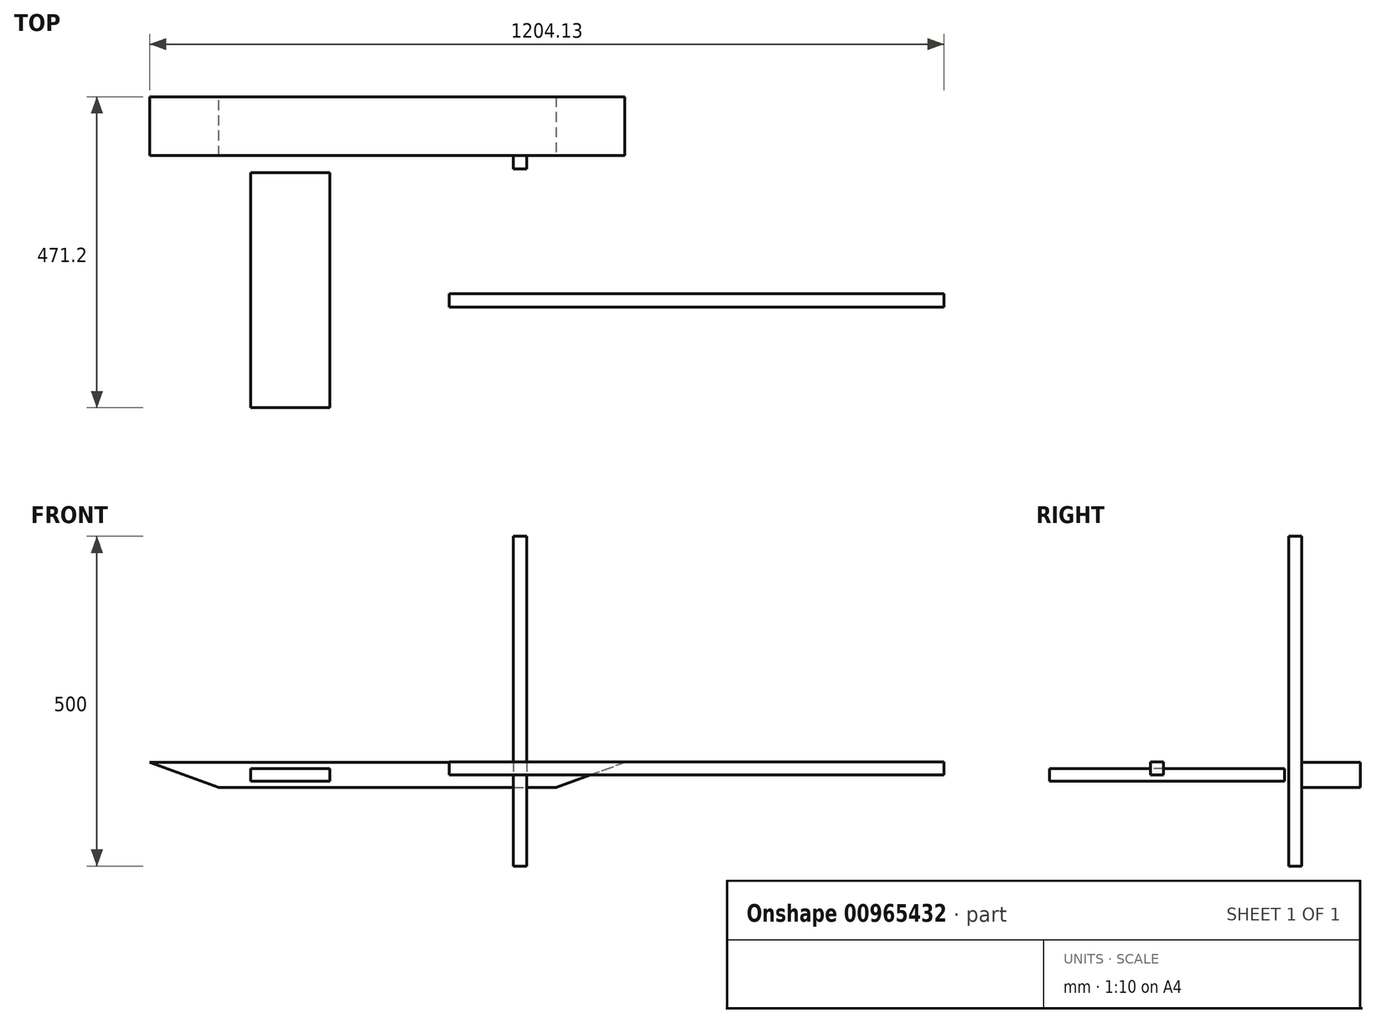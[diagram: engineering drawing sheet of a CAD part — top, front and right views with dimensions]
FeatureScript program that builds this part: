
annotation { "Feature Type Name" : "Feature", "Feature Type Description" : "" }
export const myFeature = defineFeature(function(context is Context, id is Id, definition is map)
    precondition{}
    {
        {
            var Q0;
            Q0=qCreatedBy(makeId("Top.planeOp"),FACE);
            var sketch = newSketch(context, id + "F0", { "sketchPlane" : qUnion([Q0])});
            skLineSegment(sketch, "E0.bottom", {"start": v(-376.36, 89) * mm, "end": v(343.64, 89) * mm});
            skLineSegment(sketch, "E0.top", {"start": v(-376.36, 0) * mm, "end": v(343.64, 0) * mm});
            skLineSegment(sketch, "E0.left", {"start": v(-376.36, 89) * mm, "end": v(-376.36, 0) * mm});
            skLineSegment(sketch, "E0.right", {"start": v(343.64, 89) * mm, "end": v(343.64, 0) * mm});
            skSolve(sketch);
        }
        {
            var Q0;
            Q0 = qSketchRegion(id + "F0", true);
            extrude(context, id + "F1", {"entities" : qUnion([Q0]), "endBound" : BoundingType.SYMMETRIC, "depth" : 38 * mm, "offsetDistance" : 25 * mm});
        }
        {
            var Q0;
            Q0=qCreatedBy(makeId("Top.planeOp"),FACE);
            var sketch = newSketch(context, id + "F2", { "sketchPlane" : qUnion([Q0])});
            skLineSegment(sketch, "E1.bottom", {"start": v(-223.4, -26.2) * mm, "end": v(-103.4, -26.2) * mm});
            skLineSegment(sketch, "E1.top", {"start": v(-223.4, -382.2) * mm, "end": v(-103.4, -382.2) * mm});
            skLineSegment(sketch, "E1.left", {"start": v(-223.4, -26.2) * mm, "end": v(-223.4, -382.2) * mm});
            skLineSegment(sketch, "E1.right", {"start": v(-103.4, -26.2) * mm, "end": v(-103.4, -382.2) * mm});
            skSolve(sketch);
        }
        {
            var Q0;
            Q0 = qSketchRegion(id + "F2", true);
            extrude(context, id + "F3", {"entities" : qUnion([Q0]), "endBound" : BoundingType.SYMMETRIC, "depth" : 19 * mm, "offsetDistance" : 25 * mm});
        }
        {
            var Q0;
            Q0=makeQuery(id+"F1.opExtrude","CAP_EDGE",EDGE,{"disambiguationData":[OSD([sQuery(id+"F0.wireOp",EDGE,"E0.left")])],"isStart":true});
            var Q1;
            Q1=makeQuery(id+"F1.opExtrude","CAP_EDGE",EDGE,{"disambiguationData":[OSD([sQuery(id+"F0.wireOp",EDGE,"E0.right")])],"isStart":true});
            chamfer(context, id + "F4", {"entities" : qUnion([Q0, Q1]), "chamferType" : ChamferType.OFFSET_ANGLE, "width" : 38 * mm, "oppositeDirection" : false, "angle" : 70 * degree, "tangentPropagation" : true});
        }
        {
            var Q0;
            Q0=qCreatedBy(makeId("Front.planeOp"),FACE);
            var sketch = newSketch(context, id + "F5", { "sketchPlane" : qUnion([Q0])});
            skLineSegment(sketch, "E2.bottom", {"start": v(194.9, 361.96) * mm, "end": v(174.9, 361.96) * mm});
            skLineSegment(sketch, "E2.top", {"start": v(194.9, -138.04) * mm, "end": v(174.9, -138.04) * mm});
            skLineSegment(sketch, "E2.left", {"start": v(194.9, 361.96) * mm, "end": v(194.9, -138.04) * mm});
            skLineSegment(sketch, "E2.right", {"start": v(174.9, 361.96) * mm, "end": v(174.9, -138.04) * mm});
            skSolve(sketch);
        }
        {
            var Q0;
            Q0 = qSketchRegion(id + "F5", true);
            extrude(context, id + "F6", {"entities" : qUnion([Q0]), "depth" : 20 * mm, "offsetDistance" : 25 * mm});
        }
        {
            var Q0;
            Q0=qCreatedBy(makeId("Top.planeOp"),FACE);
            var sketch = newSketch(context, id + "F7", { "sketchPlane" : qUnion([Q0])});
            skLineSegment(sketch, "E3.bottom", {"start": v(827.77, -229.48) * mm, "end": v(77.77, -229.48) * mm});
            skLineSegment(sketch, "E3.top", {"start": v(827.77, -209.48) * mm, "end": v(77.77, -209.48) * mm});
            skLineSegment(sketch, "E3.left", {"start": v(827.77, -229.48) * mm, "end": v(827.77, -209.48) * mm});
            skLineSegment(sketch, "E3.right", {"start": v(77.77, -229.48) * mm, "end": v(77.77, -209.48) * mm});
            skSolve(sketch);
        }
        {
            var Q0;
            Q0=makeQuery(id+"F7.imprint","IMPRINT",FACE,{"disambiguationData":[TD([[makeQuery(id+"F7.imprint","IMPRINT",EDGE,{"derivedFrom":sQuery(id+"F7.wireOp",EDGE,"E3.bottom")}),-1.0]])]});
            extrude(context, id + "F8", {"entities" : qUnion([Q0]), "depth" : 20 * mm, "offsetDistance" : 25 * mm});
        }
    });
